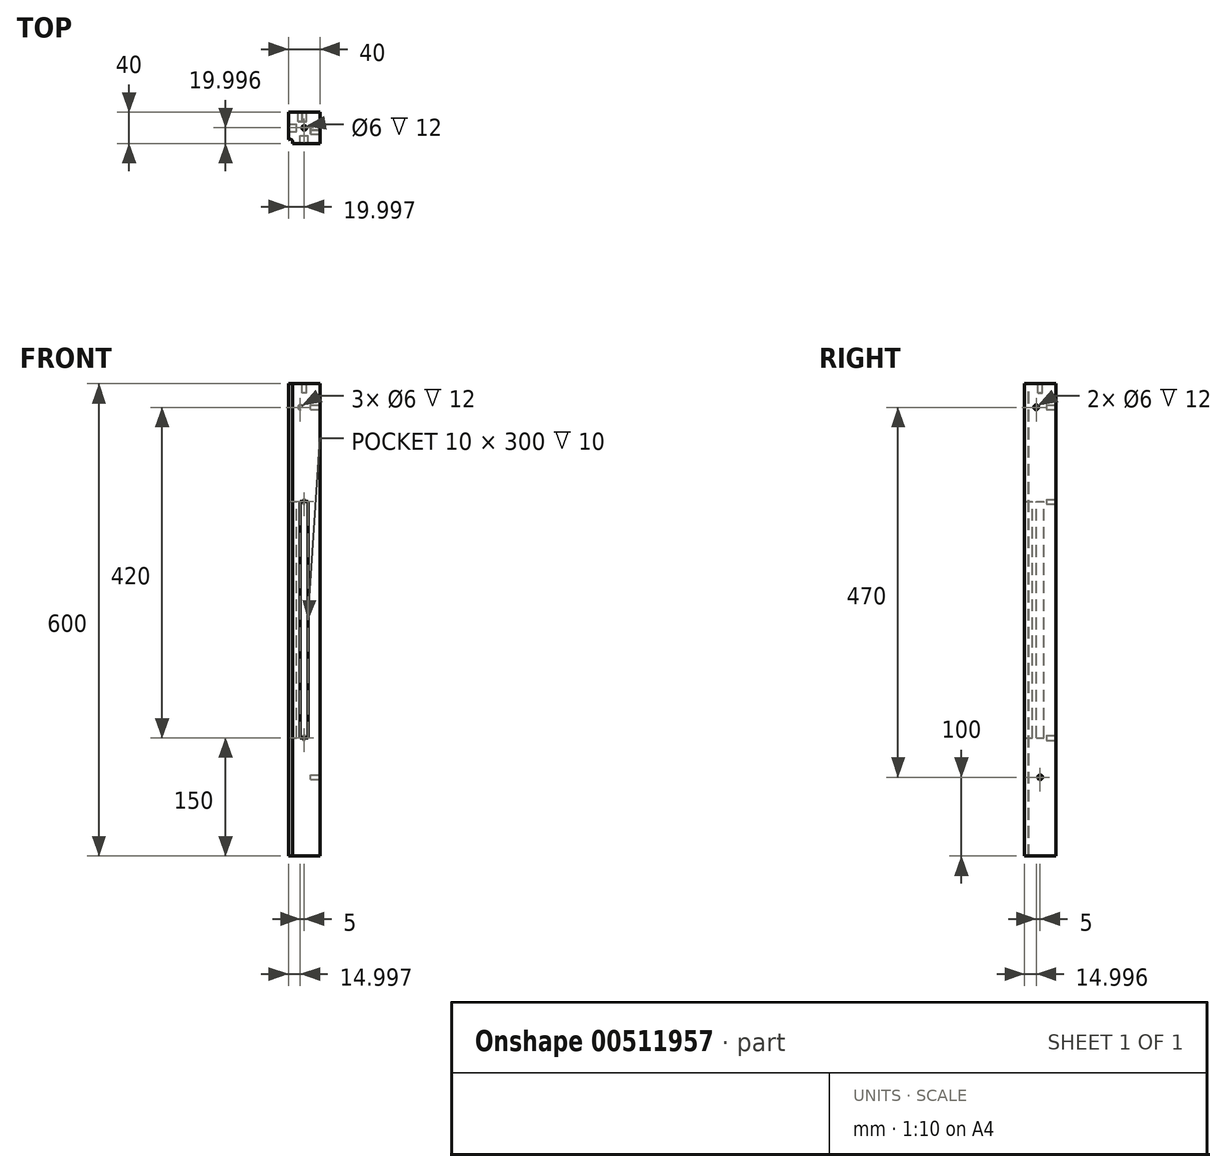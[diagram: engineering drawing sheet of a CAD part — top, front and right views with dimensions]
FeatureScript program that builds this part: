
annotation { "Feature Type Name" : "Feature", "Feature Type Description" : "" }
export const myFeature = defineFeature(function(context is Context, id is Id, definition is map)
    precondition{}
    {
        {
            var Q0;
            Q0=qCreatedBy(makeId("Top.planeOp"),FACE);
            var sketch = newSketch(context, id + "F0", { "sketchPlane" : qUnion([Q0])});
            skLineSegment(sketch, "E0.bottom", {"start": v(-52.47, 52.39) * mm, "end": v(-12.47, 52.39) * mm});
            skLineSegment(sketch, "E0.top", {"start": v(-52.47, 12.39) * mm, "end": v(-12.47, 12.39) * mm});
            skLineSegment(sketch, "E0.left", {"start": v(-52.47, 52.39) * mm, "end": v(-52.47, 12.39) * mm});
            skLineSegment(sketch, "E0.right", {"start": v(-12.47, 52.39) * mm, "end": v(-12.47, 12.39) * mm});
            skSolve(sketch);
        }
        {
            var Q0;
            Q0=makeQuery(id+"F0.imprint","IMPRINT",FACE,{"disambiguationData":[TD([[makeQuery(id+"F0.imprint","IMPRINT",EDGE,{"derivedFrom":sQuery(id+"F0.wireOp",EDGE,"E0.bottom")}),-1.0]])]});
            extrude(context, id + "F1", {"entities" : qUnion([Q0]), "depth" : 600 * mm, "offsetDistance" : 25 * mm});
        }
        {
            var Q0;
            Q0=makeQuery(id+"F1.opExtrude","SWEPT_FACE",FACE,{"disambiguationData":[OSD([sQuery(id+"F0.wireOp",EDGE,"E0.right")])]});
            var sketch = newSketch(context, id + "F2", { "sketchPlane" : qUnion([Q0])});
            skCircle(sketch, "E1", {"center": v(27.39, 570) * mm, "radius": 3 * mm});
            skSolve(sketch);
        }
        {
            var Q0;
            Q0=makeQuery(id+"F2.imprint","IMPRINT",FACE,{"disambiguationData":[TD([[makeQuery(id+"F2.imprint","IMPRINT",EDGE,{"derivedFrom":sQuery(id+"F2.wireOp",EDGE,"E1")}),1.0]])]});
            extrude(context, id + "F3", {"entities" : qUnion([Q0]), "operationType" : NewBodyOperationType.REMOVE, "oppositeDirection" : true, "depth" : 12 * mm, "offsetDistance" : 25 * mm});
        }
        {
            var Q0;
            Q0=makeQuery(id+"F1.opExtrude","SWEPT_FACE",FACE,{"disambiguationData":[OSD([sQuery(id+"F0.wireOp",EDGE,"E0.bottom")])]});
            var sketch = newSketch(context, id + "F4", { "sketchPlane" : qUnion([Q0])});
            skCircle(sketch, "E2", {"center": v(37.47, 570) * mm, "radius": 3 * mm});
            skCircle(sketch, "E3", {"center": v(32.47, 450) * mm, "radius": 3 * mm});
            skSolve(sketch);
        }
        {
            var Q0;
            Q0=makeQuery(id+"F4.imprint","IMPRINT",FACE,{"disambiguationData":[TD([[makeQuery(id+"F4.imprint","IMPRINT",EDGE,{"derivedFrom":sQuery(id+"F4.wireOp",EDGE,"E2")}),1.0]])]});
            extrude(context, id + "F5", {"entities" : qUnion([Q0]), "operationType" : NewBodyOperationType.REMOVE, "oppositeDirection" : true, "depth" : 12 * mm, "offsetDistance" : 25 * mm});
        }
        {
            var Q0;
            Q0=makeQuery(id+"F1.opExtrude","CAP_FACE",FACE,{"disambiguationData":[OSD([sQuery(id+"F0.wireOp",EDGE,"E0.bottom"),sQuery(id+"F0.wireOp",EDGE,"E0.top"),sQuery(id+"F0.wireOp",EDGE,"E0.left"),sQuery(id+"F0.wireOp",EDGE,"E0.right")])],"isStart":false});
            var sketch = newSketch(context, id + "F6", { "sketchPlane" : qUnion([Q0])});
            skCircle(sketch, "E4", {"center": v(-50.47, 14.39) * mm, "radius": 3.54 * mm});
            skSolve(sketch);
        }
        {
            var Q0;
            {var subQ0=sQuery(id+"F6.wireOp",EDGE,"E4");var subQ1=makeQuery(id+"F1.opExtrude","CAP_EDGE",EDGE,{"disambiguationData":[OSD([sQuery(id+"F0.wireOp",EDGE,"E0.top")])],"isStart":false});var subQ2=makeQuery(id+"F6.imprint","INTERSECT",VERTEX,{"derivedFrom":[subQ1,subQ0]});Q0=makeQuery(id+"F6.imprint","IMPRINT",FACE,{"disambiguationData":[TD([[makeQuery(id+"F6.imprint","IMPRINT",EDGE,{"disambiguationData":[TD([[subQ2,-1.0]])],"derivedFrom":subQ0}),1.0]])]});}
            extrude(context, id + "F7", {"entities" : qUnion([Q0]), "operationType" : NewBodyOperationType.REMOVE, "oppositeDirection" : true, "depth" : 600 * mm, "offsetDistance" : 25 * mm});
        }
        {
            var Q0;
            Q0=makeQuery(id+"F1.opExtrude","CAP_FACE",FACE,{"disambiguationData":[OSD([sQuery(id+"F0.wireOp",EDGE,"E0.bottom"),sQuery(id+"F0.wireOp",EDGE,"E0.top"),sQuery(id+"F0.wireOp",EDGE,"E0.left"),sQuery(id+"F0.wireOp",EDGE,"E0.right")])],"isStart":false});
            var sketch = newSketch(context, id + "F8", { "sketchPlane" : qUnion([Q0])});
            skPoint(sketch, "E5.centerSnap0", {"position": v(-52.47, 34.85) * mm});
            skPoint(sketch, "E5.centerSnap1", {"position": v(-32.47, 52.39) * mm});
            skCircle(sketch, "E6", {"center": v(-32.47, 32.39) * mm, "radius": 3 * mm});
            skSolve(sketch);
        }
        {
            var Q0;
            Q0=makeQuery(id+"F8.imprint","IMPRINT",FACE,{"disambiguationData":[TD([[makeQuery(id+"F8.imprint","IMPRINT",EDGE,{"derivedFrom":sQuery(id+"F8.wireOp",EDGE,"E6")}),1.0]])]});
            extrude(context, id + "F9", {"entities" : qUnion([Q0]), "operationType" : NewBodyOperationType.REMOVE, "oppositeDirection" : true, "depth" : 12 * mm, "offsetDistance" : 25 * mm});
        }
        {
            var Q0;
            Q0=makeQuery(id+"F4.imprint","IMPRINT",FACE,{"disambiguationData":[TD([[makeQuery(id+"F4.imprint","IMPRINT",EDGE,{"derivedFrom":sQuery(id+"F4.wireOp",EDGE,"E3")}),1.0]])]});
            var Q1;
            Q1=sQuery(id+"F4.wireOp",EDGE,"E3");
            extrude(context, id + "F10", {"entities" : qUnion([Q0]), "operationType" : NewBodyOperationType.REMOVE, "surfaceEntities" : qUnion([Q1]), "oppositeDirection" : true, "depth" : 12 * mm, "offsetDistance" : 25 * mm});
        }
        {
            var Q0;
            Q0=makeQuery(id+"F4.imprint","IMPRINT",FACE,{"disambiguationData":[TD([[makeQuery(id+"F4.imprint","IMPRINT",EDGE,{"derivedFrom":sQuery(id+"F4.wireOp",EDGE,"E2")}),-1.0]])]});
            var sketch = newSketch(context, id + "F11", { "sketchPlane" : qUnion([Q0])});
            skCircle(sketch, "E7", {"center": v(32.47, 150) * mm, "radius": 3 * mm});
            skSolve(sketch);
        }
        {
            var Q0;
            Q0=makeQuery(id+"F11.imprint","IMPRINT",FACE,{"disambiguationData":[TD([[makeQuery(id+"F11.imprint","IMPRINT",EDGE,{"derivedFrom":sQuery(id+"F11.wireOp",EDGE,"E7")}),1.0]])]});
            extrude(context, id + "F12", {"entities" : qUnion([Q0]), "operationType" : NewBodyOperationType.REMOVE, "oppositeDirection" : true, "depth" : 12 * mm, "offsetDistance" : 25 * mm});
        }
        {
            var Q0;
            Q0=makeQuery(id+"F1.opExtrude","SWEPT_FACE",FACE,{"disambiguationData":[OSD([sQuery(id+"F0.wireOp",EDGE,"E0.right")])]});
            var sketch = newSketch(context, id + "F13", { "sketchPlane" : qUnion([Q0])});
            skCircle(sketch, "E8", {"center": v(32.39, 100) * mm, "radius": 3 * mm});
            skSolve(sketch);
        }
        {
            var Q0;
            Q0=makeQuery(id+"F13.imprint","IMPRINT",FACE,{"disambiguationData":[TD([[makeQuery(id+"F13.imprint","IMPRINT",EDGE,{"derivedFrom":sQuery(id+"F13.wireOp",EDGE,"E8")}),1.0]])]});
            extrude(context, id + "F14", {"entities" : qUnion([Q0]), "operationType" : NewBodyOperationType.REMOVE, "oppositeDirection" : true, "depth" : 12 * mm, "offsetDistance" : 25 * mm});
        }
        {
            var Q0;
            Q0=makeQuery(id+"F0.imprint","IMPRINT",FACE,{"disambiguationData":[TD([[makeQuery(id+"F0.imprint","IMPRINT",EDGE,{"derivedFrom":sQuery(id+"F0.wireOp",EDGE,"E0.bottom")}),-1.0]])]});
            cPlane(context, id + "F15", {"entities" : qUnion([Q0]), "cplaneType" : CPlaneType.OFFSET, "offset" : 450 * mm, "width" : 150 * mm, "height" : 150 * mm});
        }
        {
            var Q0;
            Q0=qCreatedBy(id+"F15.planeOp",FACE);
            var sketch = newSketch(context, id + "F16", { "sketchPlane" : qUnion([Q0])});
            skLineSegment(sketch, "E9.bottom", {"start": v(-37.47, 12.39) * mm, "end": v(-27.47, 12.39) * mm});
            skLineSegment(sketch, "E9.top", {"start": v(-37.47, 22.39) * mm, "end": v(-27.47, 22.39) * mm});
            skLineSegment(sketch, "E9.left", {"start": v(-37.47, 12.39) * mm, "end": v(-37.47, 22.39) * mm});
            skLineSegment(sketch, "E9.right", {"start": v(-27.47, 12.39) * mm, "end": v(-27.47, 22.39) * mm});
            skLineSegment(sketch, "E10.bottom", {"start": v(-52.47, 27.39) * mm, "end": v(-42.47, 27.39) * mm});
            skLineSegment(sketch, "E10.top", {"start": v(-52.47, 37.39) * mm, "end": v(-42.47, 37.39) * mm});
            skLineSegment(sketch, "E10.left", {"start": v(-52.47, 27.39) * mm, "end": v(-52.47, 37.39) * mm});
            skLineSegment(sketch, "E10.right", {"start": v(-42.47, 27.39) * mm, "end": v(-42.47, 37.39) * mm});
            skSolve(sketch);
        }
        {
            var Q0;
            Q0=makeQuery(id+"F16.imprint","IMPRINT",FACE,{"disambiguationData":[TD([[makeQuery(id+"F16.imprint","IMPRINT",EDGE,{"derivedFrom":sQuery(id+"F16.wireOp",EDGE,"E10.bottom")}),1.0]])]});
            extrude(context, id + "F17", {"entities" : qUnion([Q0]), "operationType" : NewBodyOperationType.REMOVE, "oppositeDirection" : true, "depth" : 300 * mm, "offsetDistance" : 25 * mm});
        }
        {
            var Q0;
            Q0=makeQuery(id+"F16.imprint","IMPRINT",FACE,{"disambiguationData":[TD([[makeQuery(id+"F16.imprint","IMPRINT",EDGE,{"derivedFrom":sQuery(id+"F16.wireOp",EDGE,"E9.bottom")}),1.0]])]});
            extrude(context, id + "F18", {"entities" : qUnion([Q0]), "operationType" : NewBodyOperationType.REMOVE, "oppositeDirection" : true, "depth" : 300 * mm, "offsetDistance" : 25 * mm});
        }
    });
